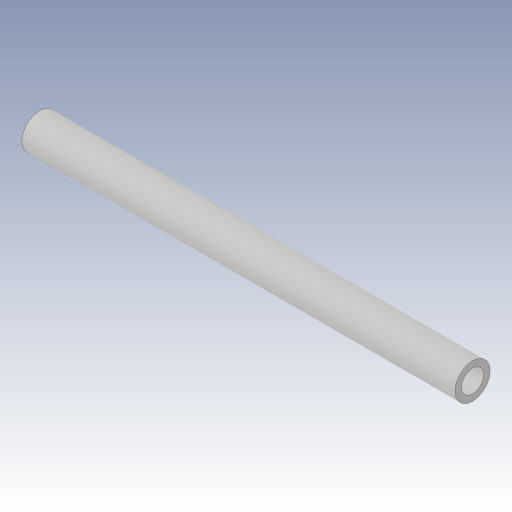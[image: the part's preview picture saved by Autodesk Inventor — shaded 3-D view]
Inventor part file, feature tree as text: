
AUTODESK INVENTOR PART (.ipt)
format: ipt  version: 2023.3 (Build 273359000, 359)  size: 117,760 bytes
history: native  units: in
note: dims shown in document units (in); Inventor stores cm internally (conversion verified against a paired STEP export)
features: extrude x1, sketch x1
ambient origin geometry x8: Origin, YZ Plane, XZ Plane, XY Plane, X Axis, Y Axis, Z Axis, Center Point
bodies: Body1 (feature_tree)
feature tree (2):
  extrude  "Extrusion3"  Depth=0.5315in
  sketch  "Skizze3"  dims[d4=0.0276in d5=0.0433in d6=0.5315in d7=0.0in]
